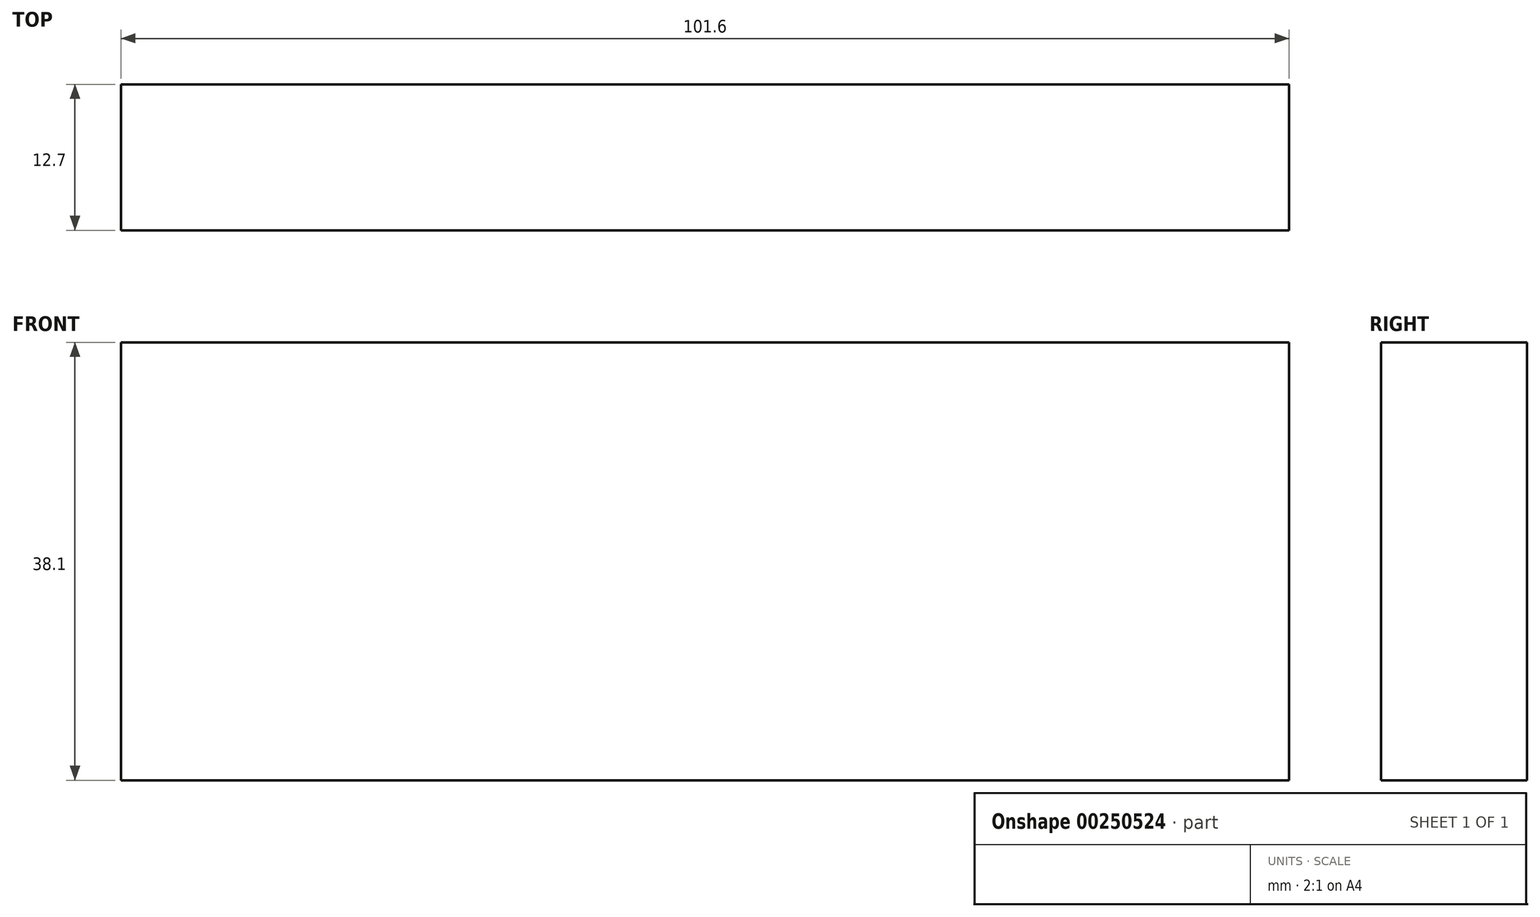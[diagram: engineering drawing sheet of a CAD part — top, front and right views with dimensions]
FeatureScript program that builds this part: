
annotation { "Feature Type Name" : "Feature", "Feature Type Description" : "" }
export const myFeature = defineFeature(function(context is Context, id is Id, definition is map)
    precondition{}
    {
        {
            var Q0;
            Q0=qCreatedBy(makeId("Front.planeOp"),FACE);
            var sketch = newSketch(context, id + "F0", { "sketchPlane" : qUnion([Q0])});
            skLineSegment(sketch, "E0.bottom", {"start": v(-50.8, 19.05) * mm, "end": v(50.8, 19.05) * mm});
            skLineSegment(sketch, "E0.top", {"start": v(-50.8, -19.05) * mm, "end": v(50.8, -19.05) * mm});
            skLineSegment(sketch, "E0.left", {"start": v(-50.8, 19.05) * mm, "end": v(-50.8, -19.05) * mm});
            skLineSegment(sketch, "E0.right", {"start": v(50.8, 19.05) * mm, "end": v(50.8, -19.05) * mm});
            skPoint(sketch, "E0.middle", {"position": v(0, 0) * mm});
            skSolve(sketch);
        }
        {
            var Q0;
            Q0 = qSketchRegion(id + "F0", true);
            extrude(context, id + "F1", {"entities" : qUnion([Q0]), "depth" : 12.7 * mm});
        }
    });
